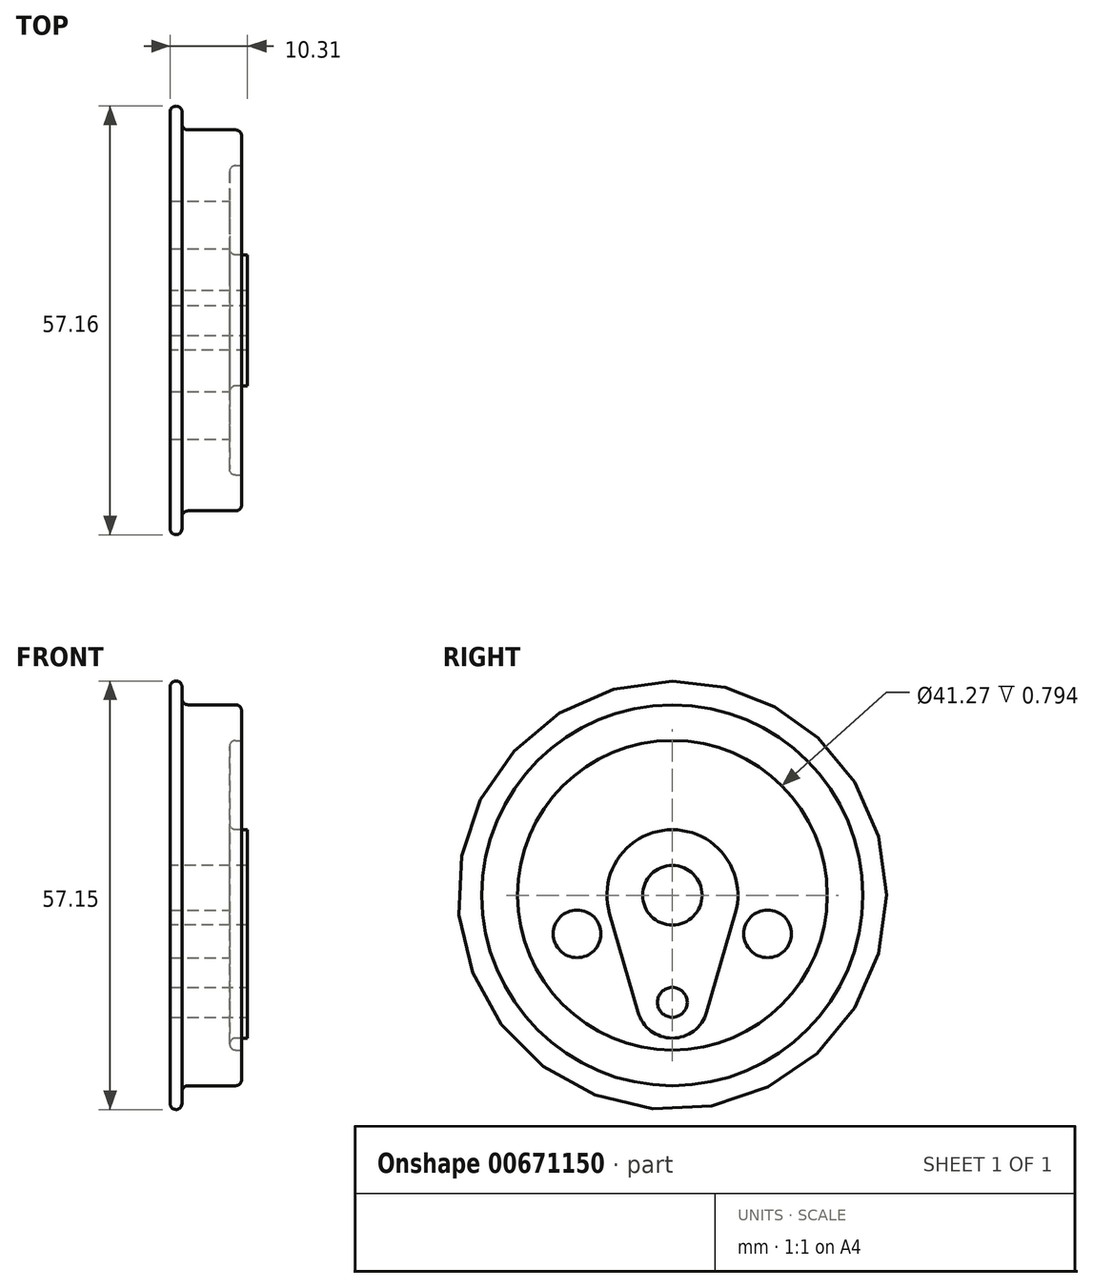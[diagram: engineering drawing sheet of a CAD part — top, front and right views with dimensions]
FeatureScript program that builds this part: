
annotation { "Feature Type Name" : "Feature", "Feature Type Description" : "" }
export const myFeature = defineFeature(function(context is Context, id is Id, definition is map)
    precondition{}
    {
        {
            var Q0;
            Q0=qCreatedBy(makeId("Front.planeOp"),FACE);
            var sketch = newSketch(context, id + "F0", { "sketchPlane" : qUnion([Q0])});
            skLineSegment(sketch, "E0", {"start": v(10.6, 36.32) * mm, "end": v(33.48, 36.32) * mm});
            skLineSegment(sketch, "E1", {"start": v(10.6, 36.32) * mm, "end": v(10.6, 8.53) * mm});
            skLineSegment(sketch, "E2", {"start": v(11.39, 7.74) * mm, "end": v(11.39, 7.74) * mm});
            skLineSegment(sketch, "E3", {"start": v(12.18, 8.53) * mm, "end": v(12.18, 10.12) * mm});
            skLineSegment(sketch, "E4", {"start": v(12.98, 10.92) * mm, "end": v(19.33, 10.92) * mm});
            skPoint(sketch, "E5.visualSharp", {"position": v(10.6, 7.74) * mm});
            skArc(sketch, "E5.filletArc", {"start": v(10.6, 8.53) * mm, "mid": v(10.83, 7.97) * mm, "end": v(11.39, 7.74) * mm});
            skPoint(sketch, "E6.visualSharp", {"position": v(12.18, 7.74) * mm});
            skArc(sketch, "E6.filletArc", {"start": v(11.39, 7.74) * mm, "mid": v(11.95, 7.97) * mm, "end": v(12.18, 8.53) * mm});
            skPoint(sketch, "E7.visualSharp", {"position": v(12.18, 10.92) * mm});
            skArc(sketch, "E7.filletArc", {"start": v(12.98, 10.92) * mm, "mid": v(12.42, 10.68) * mm, "end": v(12.18, 10.12) * mm});
            skLineSegment(sketch, "E8", {"start": v(20.12, 11.7) * mm, "end": v(20.12, 32.35) * mm});
            skLineSegment(sketch, "E9", {"start": v(20.12, 32.35) * mm, "end": v(10.6, 32.35) * mm});
            skPoint(sketch, "E10.visualSharp", {"position": v(20.12, 10.92) * mm});
            skArc(sketch, "E10.filletArc", {"start": v(19.33, 10.92) * mm, "mid": v(19.89, 11.15) * mm, "end": v(20.12, 11.7) * mm});
            skSolve(sketch);
        }
        {
            var Q0;
            Q0=qSketchRegion(id+"F0",true);
            var Q1;
            Q1=sQuery(id+"F0.wireOp",EDGE,"E0");
            revolve(context, id + "F1", {"entities" : qUnion([Q0]), "axis" : qUnion([Q1]), "revolveType" : RevolveType.FULL});
        }
        {
            var Q0;
            Q0=makeQuery(id+"F1.opRevolve","SWEPT_FACE",FACE,{"disambiguationData":[OSD([sQuery(id+"F0.wireOp",EDGE,"E8")])]});
            var sketch = newSketch(context, id + "F2", { "sketchPlane" : qUnion([Q0])});
            skCircle(sketch, "E11", {"center": v(0, 36.32) * mm, "radius": 8.73 * mm});
            skCircle(sketch, "E12", {"center": v(0, 22.03) * mm, "radius": 1.98 * mm});
            skCircle(sketch, "E13", {"center": v(0, 22.03) * mm, "radius": 4.76 * mm});
            skCircle(sketch, "E14", {"center": v(0, 36.32) * mm, "radius": 19.05 * mm});
            skLineSegment(sketch, "E15", {"start": v(-8.39, 33.9) * mm, "end": v(-4.58, 20.7) * mm});
            skLineSegment(sketch, "E16", {"start": v(4.58, 20.7) * mm, "end": v(8.39, 33.9) * mm});
            skSolve(sketch);
        }
        {
            var Q0;
            Q0=makeQuery(id+"F2.imprint","IMPRINT",FACE,{"disambiguationData":[TD([[makeQuery(id+"F2.imprint","IMPRINT",EDGE,{"derivedFrom":sQuery(id+"F2.wireOp",EDGE,"E12")}),-1.0]])]});
            var Q1;
            {var subQ0=sQuery(id+"F2.wireOp",EDGE,"E15");Q1=makeQuery(id+"F2.imprint","IMPRINT",FACE,{"disambiguationData":[TD([[makeQuery(id+"F2.imprint","IMPRINT",EDGE,{"derivedFrom":subQ0}),1.0]])]});}
            var Q2;
            Q2=makeQuery(id+"F2.imprint","IMPRINT",FACE,{"disambiguationData":[TD([[makeQuery(id+"F2.imprint","IMPRINT",EDGE,{"derivedFrom":makeQuery(id+"F1.opRevolve","SWEPT_EDGE",EDGE,{"disambiguationData":[OSD([sQuery(id+"F0.wireOp",EDGE,"E8"),sQuery(id+"F0.wireOp",EDGE,"E9")])]})}),1.0]])]});
            var Q3;
            Q3=makeQuery(id+"F2.imprint","IMPRINT",FACE,{"disambiguationData":[TD([[makeQuery(id+"F2.imprint","IMPRINT",EDGE,{"derivedFrom":sQuery(id+"F2.wireOp",EDGE,"E12")}),1.0]])]});
            extrude(context, id + "F3", {"entities" : qUnion([Q0, Q1, Q2, Q3]), "operationType" : NewBodyOperationType.ADD, "depth" : 0.8 * mm});
        }
        {
            var Q0;
            Q0=makeQuery(id+"F3.opExtrude","CAP_FACE",FACE,{"disambiguationData":[OSD([sQuery(id+"F0.wireOp",EDGE,"E8"),sQuery(id+"F0.wireOp",EDGE,"E9"),sQuery(id+"F2.wireOp",EDGE,"E11"),sQuery(id+"F2.wireOp",EDGE,"E13"),sQuery(id+"F2.wireOp",EDGE,"E15"),sQuery(id+"F2.wireOp",EDGE,"E16")])],"isStart":false});
            var sketch = newSketch(context, id + "F4", { "sketchPlane" : qUnion([Q0])});
            skCircle(sketch, "E17", {"center": v(0, 22.03) * mm, "radius": 1.98 * mm});
            skSolve(sketch);
        }
        {
            var Q0;
            Q0=makeQuery(id+"F4.imprint","IMPRINT",FACE,{"disambiguationData":[TD([[makeQuery(id+"F4.imprint","IMPRINT",EDGE,{"derivedFrom":sQuery(id+"F4.wireOp",EDGE,"E17")}),1.0]])]});
            extrude(context, id + "F5", {"entities" : qUnion([Q0]), "operationType" : NewBodyOperationType.REMOVE, "oppositeDirection" : true, "depth" : 25.4 * mm});
        }
        {
            var Q0;
            Q0=makeQuery(id+"F1.opRevolve","SWEPT_FACE",FACE,{"disambiguationData":[OSD([sQuery(id+"F0.wireOp",EDGE,"E8")])]});
            var sketch = newSketch(context, id + "F6", { "sketchPlane" : qUnion([Q0])});
            skCircle(sketch, "E18", {"center": v(-12.7, 31.17) * mm, "radius": 3.18 * mm});
            skCircle(sketch, "E19", {"center": v(12.7, 31.17) * mm, "radius": 3.18 * mm});
            skSolve(sketch);
        }
        {
            var Q0;
            Q0=qSketchRegion(id+"F6",true);
            extrude(context, id + "F7", {"entities" : qUnion([Q0]), "operationType" : NewBodyOperationType.REMOVE, "oppositeDirection" : true, "depth" : 25.4 * mm});
        }
        {
            var Q0;
            Q0=makeQuery(id+"F1.opRevolve","SWEPT_FACE",FACE,{"disambiguationData":[OSD([sQuery(id+"F0.wireOp",EDGE,"E8")])]});
            var sketch = newSketch(context, id + "F8", { "sketchPlane" : qUnion([Q0])});
            skCircle(sketch, "E20", {"center": v(0, 36.32) * mm, "radius": 20.64 * mm});
            skSolve(sketch);
        }
        {
            var Q0;
            Q0=makeQuery(id+"F8.imprint","IMPRINT",FACE,{"disambiguationData":[TD([[makeQuery(id+"F8.imprint","IMPRINT",EDGE,{"derivedFrom":sQuery(id+"F8.wireOp",EDGE,"E20")}),1.0]])]});
            extrude(context, id + "F9", {"entities" : qUnion([Q0]), "operationType" : NewBodyOperationType.REMOVE, "oppositeDirection" : true, "depth" : 1.59 * mm});
        }
        {
            var Q0;
            Q0=makeQuery(id+"F9.boolean.opBoolean","COPY",EDGE,{"derivedFrom":makeQuery(id+"F9.opExtrude","CAP_EDGE",EDGE,{"disambiguationData":[OSD([sQuery(id+"F8.wireOp",EDGE,"E20")])],"isStart":false})});
            var Q1;
            Q1=makeQuery(id+"F9.boolean.opBoolean","COPY",EDGE,{"derivedFrom":makeQuery(id+"F9.opExtrude","CAP_EDGE",EDGE,{"disambiguationData":[OSD([sQuery(id+"F2.wireOp",EDGE,"E16")])],"isStart":false})});
            fillet(context, id + "F10", {"entities" : qUnion([Q0, Q1]), "radius" : 0.8 * mm, "tangentPropagation" : true, "allowEdgeOverflow" : false});
        }
    });
